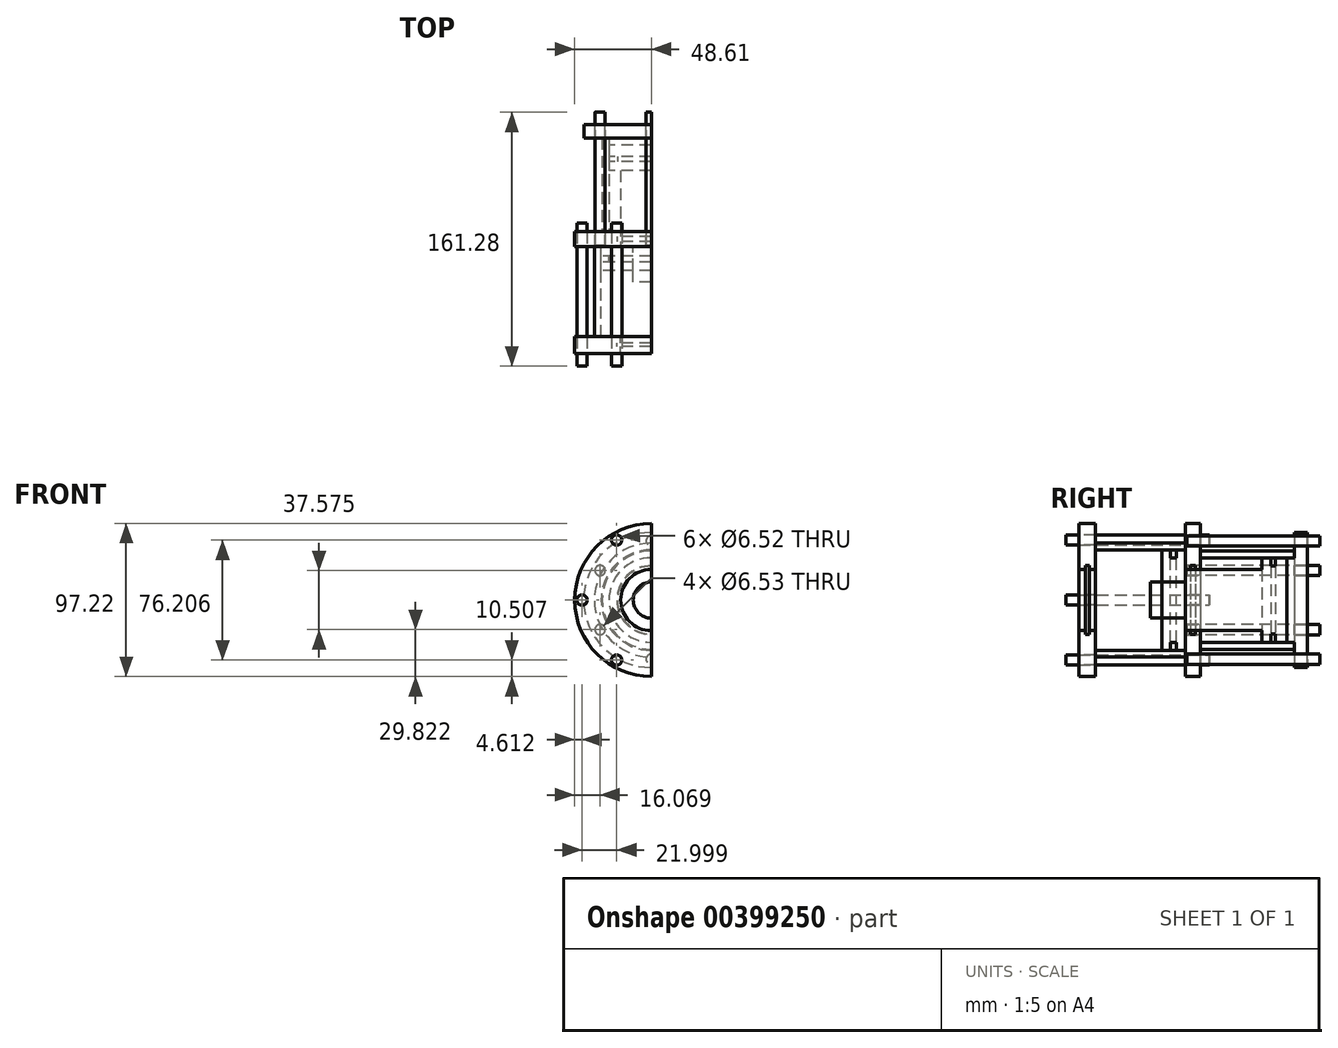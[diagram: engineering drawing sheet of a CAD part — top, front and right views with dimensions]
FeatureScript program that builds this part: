
annotation { "Feature Type Name" : "Feature", "Feature Type Description" : "" }
export const myFeature = defineFeature(function(context is Context, id is Id, definition is map)
    precondition{}
    {
        {
            var Q0;
            Q0=qCreatedBy(makeId("Right.planeOp"),FACE);
            var sketch = newSketch(context, id + "F0", { "sketchPlane" : qUnion([Q0])});
            skLineSegment(sketch, "E0.bottom", {"start": v(0, 0) * mm, "end": v(15.17, 0) * mm});
            skLineSegment(sketch, "E0.top", {"start": v(0, 31.89) * mm, "end": v(15.17, 31.89) * mm});
            skLineSegment(sketch, "E0.left", {"start": v(0, 0) * mm, "end": v(0, 31.89) * mm});
            skLineSegment(sketch, "E0.right", {"start": v(15.17, 0) * mm, "end": v(15.17, 31.89) * mm});
            skLineSegment(sketch, "E1.bottom", {"start": v(15.17, 0) * mm, "end": v(63.65, 0) * mm});
            skLineSegment(sketch, "E1.top", {"start": v(15.17, 19.4) * mm, "end": v(63.65, 19.4) * mm});
            skLineSegment(sketch, "E1.left", {"start": v(15.17, 0) * mm, "end": v(15.17, 19.4) * mm});
            skLineSegment(sketch, "E2.bottom", {"start": v(0, 0) * mm, "end": v(-58.53, 0) * mm});
            skLineSegment(sketch, "E2.top", {"start": v(0, 19.4) * mm, "end": v(-58.53, 19.4) * mm});
            skLineSegment(sketch, "E2.left", {"start": v(0, 0) * mm, "end": v(0, 19.4) * mm});
            skLineSegment(sketch, "E2.right", {"start": v(-58.53, 0) * mm, "end": v(-58.53, 19.4) * mm});
            skLineSegment(sketch, "E3.bottom", {"start": v(15.17, 19.4) * mm, "end": v(24.61, 19.4) * mm});
            skLineSegment(sketch, "E3.top", {"start": v(15.17, 48.61) * mm, "end": v(24.61, 48.61) * mm});
            skLineSegment(sketch, "E3.left", {"start": v(15.17, 19.4) * mm, "end": v(15.17, 48.61) * mm});
            skLineSegment(sketch, "E3.right", {"start": v(24.61, 19.4) * mm, "end": v(24.61, 48.61) * mm});
            skLineSegment(sketch, "E4.bottom", {"start": v(15.17, 31.89) * mm, "end": v(-42, 31.89) * mm});
            skLineSegment(sketch, "E4.top", {"start": v(15.17, 36.17) * mm, "end": v(-42, 36.17) * mm});
            skLineSegment(sketch, "E4.left", {"start": v(15.17, 31.89) * mm, "end": v(15.17, 36.17) * mm});
            skLineSegment(sketch, "E4.right", {"start": v(-42, 31.89) * mm, "end": v(-42, 36.17) * mm});
            skLineSegment(sketch, "E5.bottom", {"start": v(-42, 19.4) * mm, "end": v(-52.7, 19.4) * mm});
            skLineSegment(sketch, "E5.top", {"start": v(-42, 48.61) * mm, "end": v(-52.7, 48.61) * mm});
            skLineSegment(sketch, "E5.left", {"start": v(-42, 19.4) * mm, "end": v(-42, 48.61) * mm});
            skLineSegment(sketch, "E5.right", {"start": v(-52.7, 19.4) * mm, "end": v(-52.7, 48.61) * mm});
            skLineSegment(sketch, "E6.bottom", {"start": v(63.65, 0) * mm, "end": v(84.26, 0) * mm});
            skLineSegment(sketch, "E6.top", {"start": v(63.65, 26.83) * mm, "end": v(84.26, 26.83) * mm});
            skLineSegment(sketch, "E6.left", {"start": v(63.65, 0) * mm, "end": v(63.65, 26.83) * mm});
            skLineSegment(sketch, "E7.bottom", {"start": v(84.26, 0) * mm, "end": v(92.59, 0) * mm});
            skLineSegment(sketch, "E7.top", {"start": v(84.26, 42.86) * mm, "end": v(92.59, 42.86) * mm});
            skLineSegment(sketch, "E7.left", {"start": v(84.26, 26.83) * mm, "end": v(84.26, 42.86) * mm});
            skLineSegment(sketch, "E7.right", {"start": v(92.59, 0) * mm, "end": v(92.59, 42.86) * mm});
            skLineSegment(sketch, "E8.bottom", {"start": v(-48.36, 19.4) * mm, "end": v(-45.88, 19.4) * mm});
            skLineSegment(sketch, "E8.top", {"start": v(-48.36, 21.88) * mm, "end": v(-45.88, 21.88) * mm});
            skLineSegment(sketch, "E8.left", {"start": v(-48.36, 19.4) * mm, "end": v(-48.36, 21.88) * mm});
            skLineSegment(sketch, "E8.right", {"start": v(-45.88, 19.4) * mm, "end": v(-45.88, 21.88) * mm});
            skLineSegment(sketch, "E9.bottom", {"start": v(18.28, 19.4) * mm, "end": v(21.52, 19.4) * mm});
            skLineSegment(sketch, "E9.top", {"start": v(18.28, 21.88) * mm, "end": v(21.52, 21.88) * mm});
            skLineSegment(sketch, "E9.left", {"start": v(18.28, 19.4) * mm, "end": v(18.28, 21.88) * mm});
            skLineSegment(sketch, "E9.right", {"start": v(21.52, 19.4) * mm, "end": v(21.52, 21.88) * mm});
            skLineSegment(sketch, "E10.bottom", {"start": v(5.47, 31.89) * mm, "end": v(9.23, 31.89) * mm});
            skLineSegment(sketch, "E10.top", {"start": v(5.47, 26.83) * mm, "end": v(9.23, 26.83) * mm});
            skLineSegment(sketch, "E10.left", {"start": v(5.47, 31.89) * mm, "end": v(5.47, 26.83) * mm});
            skLineSegment(sketch, "E10.right", {"start": v(9.23, 31.89) * mm, "end": v(9.23, 26.83) * mm});
            skLineSegment(sketch, "E11.bottom", {"start": v(15.17, 11.47) * mm, "end": v(-7.2, 11.47) * mm});
            skLineSegment(sketch, "E11.top", {"start": v(15.17, 0) * mm, "end": v(-7.2, 0) * mm});
            skLineSegment(sketch, "E11.left", {"start": v(15.17, 11.47) * mm, "end": v(15.17, 0) * mm});
            skLineSegment(sketch, "E11.right", {"start": v(-7.2, 11.47) * mm, "end": v(-7.2, 0) * mm});
            skLineSegment(sketch, "E12.bottom", {"start": v(84.26, 26.83) * mm, "end": v(79.61, 26.83) * mm});
            skLineSegment(sketch, "E12.top", {"start": v(82.48, 0) * mm, "end": v(79.61, 0) * mm});
            skLineSegment(sketch, "E12.right", {"start": v(79.61, 26.83) * mm, "end": v(79.61, 0) * mm});
            skLineSegment(sketch, "E13.bottom", {"start": v(84.26, 26.83) * mm, "end": v(24.61, 26.83) * mm});
            skLineSegment(sketch, "E13.top", {"start": v(84.26, 31.23) * mm, "end": v(24.61, 31.23) * mm});
            skLineSegment(sketch, "E13.left", {"start": v(84.26, 26.83) * mm, "end": v(84.26, 31.23) * mm});
            skLineSegment(sketch, "E13.right", {"start": v(24.61, 26.83) * mm, "end": v(24.61, 31.23) * mm});
            skLineSegment(sketch, "E14.bottom", {"start": v(69.32, 26.83) * mm, "end": v(72.3, 26.83) * mm});
            skLineSegment(sketch, "E14.top", {"start": v(69.32, 21.56) * mm, "end": v(72.3, 21.56) * mm});
            skLineSegment(sketch, "E14.left", {"start": v(69.32, 26.83) * mm, "end": v(69.32, 21.56) * mm});
            skLineSegment(sketch, "E14.right", {"start": v(72.3, 26.83) * mm, "end": v(72.3, 21.56) * mm});
            skSolve(sketch);
        }
        {
            var Q0;
            Q0=makeQuery(id+"F0.imprint","IMPRINT",FACE,{"disambiguationData":[TD([[makeQuery(id+"F0.imprint","IMPRINT",EDGE,{"derivedFrom":sQuery(id+"F0.wireOp",EDGE,"E2.bottom")}),-1.0]])]});
            var Q1;
            {var subQ6=sQuery(id+"F0.wireOp",EDGE,"E0.left");Q1=makeQuery(id+"F0.imprint","IMPRINT",FACE,{"disambiguationData":[TD([[makeQuery(id+"F0.imprint","IMPRINT",EDGE,{"derivedFrom":subQ6}),-1.0]])]});}
            var Q2;
            Q2=sQuery(id+"F0.wireOp",EDGE,"E2.bottom");
            revolve(context, id + "F1", {"entities" : qUnion([Q0, Q1]), "axis" : qUnion([Q2]), "revolveType" : RevolveType.FULL});
        }
        {
            var Q0;
            {var subQ4=sQuery(id+"F0.wireOp",EDGE,"E1.bottom");Q0=makeQuery(id+"F0.imprint","IMPRINT",FACE,{"disambiguationData":[TD([[makeQuery(id+"F0.imprint","IMPRINT",EDGE,{"derivedFrom":subQ4}),1.0]])]});}
            var Q1;
            {var subQ5=sQuery(id+"F0.wireOp",EDGE,"E11.left");Q1=makeQuery(id+"F0.imprint","IMPRINT",FACE,{"disambiguationData":[TD([[makeQuery(id+"F0.imprint","IMPRINT",EDGE,{"derivedFrom":subQ5}),-1.0]])]});}
            var Q2;
            {var subQ4=sQuery(id+"F0.wireOp",EDGE,"E12.right");Q2=makeQuery(id+"F0.imprint","IMPRINT",FACE,{"disambiguationData":[TD([[makeQuery(id+"F0.imprint","IMPRINT",EDGE,{"derivedFrom":subQ4}),-1.0]])]});}
            var Q3;
            Q3=sQuery(id+"F0.wireOp",EDGE,"E1.bottom");
            revolve(context, id + "F2", {"entities" : qUnion([Q0, Q1, Q2]), "axis" : qUnion([Q3]), "revolveType" : RevolveType.FULL});
        }
        {
            var Q0;
            {var subQ5=sQuery(id+"F0.wireOp",EDGE,"E5.top");Q0=makeQuery(id+"F0.imprint","IMPRINT",FACE,{"disambiguationData":[TD([[makeQuery(id+"F0.imprint","IMPRINT",EDGE,{"derivedFrom":subQ5}),1.0]])]});}
            var Q1;
            Q1=sQuery(id+"F0.wireOp",EDGE,"E2.bottom");
            revolve(context, id + "F3", {"entities" : qUnion([Q0]), "axis" : qUnion([Q1]), "revolveType" : RevolveType.FULL});
        }
        {
            var Q0;
            {var subQ2=sQuery(id+"F0.wireOp",EDGE,"E3.top");Q0=makeQuery(id+"F0.imprint","IMPRINT",FACE,{"disambiguationData":[TD([[makeQuery(id+"F0.imprint","IMPRINT",EDGE,{"derivedFrom":subQ2}),-1.0]])]});}
            var Q1;
            Q1=sQuery(id+"F0.wireOp",EDGE,"E1.bottom");
            revolve(context, id + "F4", {"entities" : qUnion([Q0]), "axis" : qUnion([Q1]), "revolveType" : RevolveType.FULL});
        }
        {
            var Q0;
            {var subQ3=sQuery(id+"F0.wireOp",EDGE,"E7.bottom");Q0=makeQuery(id+"F0.imprint","IMPRINT",FACE,{"disambiguationData":[TD([[makeQuery(id+"F0.imprint","IMPRINT",EDGE,{"derivedFrom":subQ3}),1.0]])]});}
            var Q1;
            Q1=sQuery(id+"F0.wireOp",EDGE,"E1.bottom");
            revolve(context, id + "F5", {"entities" : qUnion([Q0]), "axis" : qUnion([Q1]), "revolveType" : RevolveType.FULL});
        }
        {
            var Q0;
            {var subQ0=sQuery(id+"F0.wireOp",EDGE,"E4.top");Q0=makeQuery(id+"F0.imprint","IMPRINT",FACE,{"disambiguationData":[TD([[makeQuery(id+"F0.imprint","IMPRINT",EDGE,{"derivedFrom":subQ0}),1.0]])]});}
            var Q1;
            Q1=sQuery(id+"F0.wireOp",EDGE,"E2.bottom");
            revolve(context, id + "F6", {"entities" : qUnion([Q0]), "axis" : qUnion([Q1]), "revolveType" : RevolveType.FULL});
        }
        {
            var Q0;
            Q0=makeQuery(id+"F0.imprint","IMPRINT",FACE,{"disambiguationData":[TD([[makeQuery(id+"F0.imprint","IMPRINT",EDGE,{"derivedFrom":sQuery(id+"F0.wireOp",EDGE,"E13.top")}),1.0]])]});
            var Q1;
            Q1=sQuery(id+"F0.wireOp",EDGE,"E1.bottom");
            revolve(context, id + "F7", {"entities" : qUnion([Q0]), "axis" : qUnion([Q1]), "revolveType" : RevolveType.FULL});
        }
        {
            var Q0;
            Q0=makeQuery(id+"F5.opRevolve","SWEPT_FACE",FACE,{"disambiguationData":[OSD([sQuery(id+"F0.wireOp",EDGE,"E7.right")])]});
            var sketch = newSketch(context, id + "F8", { "sketchPlane" : qUnion([Q0])});
            skCircle(sketch, "E15", {"center": v(0, 37.57) * mm, "radius": 3.27 * mm});
            skCircle(sketch, "E16.1.0", {"center": v(-32.54, 18.79) * mm, "radius": 3.27 * mm});
            skCircle(sketch, "E16.2.0", {"center": v(-32.54, -18.79) * mm, "radius": 3.27 * mm});
            skCircle(sketch, "E16.3.0", {"center": v(0, -37.57) * mm, "radius": 3.27 * mm});
            skCircle(sketch, "E16.4.0", {"center": v(32.54, -18.79) * mm, "radius": 3.27 * mm});
            skCircle(sketch, "E16.5.0", {"center": v(32.54, 18.79) * mm, "radius": 3.27 * mm});
            skPoint(sketch, "E16.center", {"position": v(0, 0) * mm});
            skSolve(sketch);
        }
        {
            var Q0;
            Q0=makeQuery(id+"F8.imprint","IMPRINT",FACE,{"disambiguationData":[TD([[makeQuery(id+"F8.imprint","IMPRINT",EDGE,{"derivedFrom":sQuery(id+"F8.wireOp",EDGE,"E16.1.0")}),1.0]])]});
            var Q1;
            Q1=makeQuery(id+"F8.imprint","IMPRINT",FACE,{"disambiguationData":[TD([[makeQuery(id+"F8.imprint","IMPRINT",EDGE,{"derivedFrom":sQuery(id+"F8.wireOp",EDGE,"E15")}),1.0]])]});
            var Q2;
            Q2=makeQuery(id+"F8.imprint","IMPRINT",FACE,{"disambiguationData":[TD([[makeQuery(id+"F8.imprint","IMPRINT",EDGE,{"derivedFrom":sQuery(id+"F8.wireOp",EDGE,"E16.5.0")}),1.0]])]});
            var Q3;
            Q3=makeQuery(id+"F8.imprint","IMPRINT",FACE,{"disambiguationData":[TD([[makeQuery(id+"F8.imprint","IMPRINT",EDGE,{"derivedFrom":sQuery(id+"F8.wireOp",EDGE,"E16.4.0")}),1.0]])]});
            var Q4;
            Q4=makeQuery(id+"F8.imprint","IMPRINT",FACE,{"disambiguationData":[TD([[makeQuery(id+"F8.imprint","IMPRINT",EDGE,{"derivedFrom":sQuery(id+"F8.wireOp",EDGE,"E16.3.0")}),1.0]])]});
            var Q5;
            Q5=makeQuery(id+"F8.imprint","IMPRINT",FACE,{"disambiguationData":[TD([[makeQuery(id+"F8.imprint","IMPRINT",EDGE,{"derivedFrom":sQuery(id+"F8.wireOp",EDGE,"E16.2.0")}),1.0]])]});
            var Q6;
            Q6=makeQuery(id+"F4.opRevolve","SWEPT_FACE",FACE,{"disambiguationData":[OSD([sQuery(id+"F0.wireOp",EDGE,"E3.left"),sQuery(id+"F0.wireOp",EDGE,"E4.left")])]});
            extrude(context, id + "F9", {"entities" : qUnion([Q0, Q1, Q2, Q3, Q4, Q5]), "operationType" : NewBodyOperationType.REMOVE, "endBound" : BoundingType.UP_TO_SURFACE, "oppositeDirection" : true, "endBoundEntityFace" : qUnion([Q6]), "depth" : 25 * mm});
        }
        {
            var Q0;
            Q0=makeQuery(id+"F3.opRevolve","SWEPT_FACE",FACE,{"disambiguationData":[OSD([sQuery(id+"F0.wireOp",EDGE,"E5.right")])]});
            var sketch = newSketch(context, id + "F10", { "sketchPlane" : qUnion([Q0])});
            skLineSegment(sketch, "E17", {"start": v(0, 0) * mm, "end": v(24.3, 42.1) * mm});
            skCircle(sketch, "E18", {"center": v(22, 38.1) * mm, "radius": 3.26 * mm});
            skCircle(sketch, "E19.1.0", {"center": v(-22, 38.1) * mm, "radius": 3.26 * mm});
            skCircle(sketch, "E19.2.0", {"center": v(-44, 0) * mm, "radius": 3.26 * mm});
            skCircle(sketch, "E19.3.0", {"center": v(-22, -38.1) * mm, "radius": 3.26 * mm});
            skCircle(sketch, "E19.4.0", {"center": v(22, -38.1) * mm, "radius": 3.26 * mm});
            skCircle(sketch, "E19.5.0", {"center": v(44, 0) * mm, "radius": 3.26 * mm});
            skPoint(sketch, "E19.center", {"position": v(0, 0) * mm});
            skSolve(sketch);
        }
        {
            var Q0;
            Q0=makeQuery(id+"F10.imprint","IMPRINT",FACE,{"disambiguationData":[TD([[makeQuery(id+"F10.imprint","IMPRINT",EDGE,{"derivedFrom":sQuery(id+"F10.wireOp",EDGE,"E19.1.0")}),1.0]])]});
            var Q1;
            Q1=makeQuery(id+"F10.imprint","IMPRINT",FACE,{"disambiguationData":[TD([[makeQuery(id+"F10.imprint","IMPRINT",EDGE,{"derivedFrom":sQuery(id+"F10.wireOp",EDGE,"E19.2.0")}),1.0]])]});
            var Q2;
            Q2=makeQuery(id+"F10.imprint","IMPRINT",FACE,{"disambiguationData":[TD([[makeQuery(id+"F10.imprint","IMPRINT",EDGE,{"derivedFrom":sQuery(id+"F10.wireOp",EDGE,"E19.3.0")}),1.0]])]});
            var Q3;
            Q3=makeQuery(id+"F10.imprint","IMPRINT",FACE,{"disambiguationData":[TD([[makeQuery(id+"F10.imprint","IMPRINT",EDGE,{"derivedFrom":sQuery(id+"F10.wireOp",EDGE,"E19.4.0")}),1.0]])]});
            var Q4;
            Q4=makeQuery(id+"F10.imprint","IMPRINT",FACE,{"disambiguationData":[TD([[makeQuery(id+"F10.imprint","IMPRINT",EDGE,{"derivedFrom":sQuery(id+"F10.wireOp",EDGE,"E19.5.0")}),1.0]])]});
            var Q5;
            {var subQ0=sQuery(id+"F10.wireOp",EDGE,"E18");var subQ1=sQuery(id+"F10.wireOp",EDGE,"E17");var subQ2=makeQuery(id+"F10.imprint","INTERSECT",VERTEX,{"disambiguationData":[OD(0.0)],"derivedFrom":[subQ1,subQ0]});Q5=makeQuery(id+"F10.imprint","IMPRINT",FACE,{"disambiguationData":[TD([[makeQuery(id+"F10.imprint","IMPRINT",EDGE,{"disambiguationData":[TD([[subQ2,-1.0]])],"derivedFrom":subQ1}),-1.0]])]});}
            var Q6;
            {var subQ0=sQuery(id+"F10.wireOp",EDGE,"E18");var subQ1=sQuery(id+"F10.wireOp",EDGE,"E17");var subQ2=makeQuery(id+"F10.imprint","INTERSECT",VERTEX,{"disambiguationData":[OD(0.0)],"derivedFrom":[subQ1,subQ0]});Q6=makeQuery(id+"F10.imprint","IMPRINT",FACE,{"disambiguationData":[TD([[makeQuery(id+"F10.imprint","IMPRINT",EDGE,{"disambiguationData":[TD([[subQ2,-1.0]])],"derivedFrom":subQ1}),1.0]])]});}
            var Q7;
            Q7=makeQuery(id+"F4.opRevolve","SWEPT_FACE",FACE,{"disambiguationData":[OSD([sQuery(id+"F0.wireOp",EDGE,"E3.right"),sQuery(id+"F0.wireOp",EDGE,"lStvYGKo-UQwx-T2YS-vUQB-Xu7iDgR6D970.right")])]});
            extrude(context, id + "F11", {"entities" : qUnion([Q0, Q1, Q2, Q3, Q4, Q5, Q6]), "operationType" : NewBodyOperationType.REMOVE, "endBound" : BoundingType.UP_TO_SURFACE, "oppositeDirection" : true, "endBoundEntityFace" : qUnion([Q7]), "depth" : 25 * mm});
        }
        {
            var Q0;
            Q0=makeQuery(id+"F10.imprint","IMPRINT",FACE,{"disambiguationData":[TD([[makeQuery(id+"F10.imprint","IMPRINT",EDGE,{"derivedFrom":sQuery(id+"F10.wireOp",EDGE,"E19.1.0")}),1.0]])]});
            var Q1;
            Q1=makeQuery(id+"F4.opRevolve","SWEPT_FACE",FACE,{"disambiguationData":[OSD([sQuery(id+"F0.wireOp",EDGE,"E3.right"),sQuery(id+"F0.wireOp",EDGE,"lStvYGKo-UQwx-T2YS-vUQB-Xu7iDgR6D970.right")])]});
            extrude(context, id + "F12", {"entities" : qUnion([Q0]), "depth" : 8 * mm, "hasSecondDirection" : true, "secondDirectionOppositeDirection" : true, "secondDirectionBoundEntityFace" : qUnion([Q1]), "secondDirectionDepth" : 83 * mm});
        }
        {
            var Q0;
            Q0=makeQuery(id+"F12.opExtrude","SWEPT_BODY",BODY,{"disambiguationData":[OSD([sQuery(id+"F10.wireOp",EDGE,"E19.1.0")])]});
            var Q1;
            Q1=sQuery(id+"F0.wireOp",EDGE,"E1.bottom");
            circularPattern(context, id + "F13", {"entities" : qUnion([Q0]), "axis" : qUnion([Q1]), "angle" : 360 * degree, "instanceCount" : 6, "equalSpace" : true});
        }
        {
            var Q0;
            Q0=makeQuery(id+"F8.imprint","IMPRINT",FACE,{"disambiguationData":[TD([[makeQuery(id+"F8.imprint","IMPRINT",EDGE,{"derivedFrom":sQuery(id+"F8.wireOp",EDGE,"E15")}),1.0]])]});
            extrude(context, id + "F14", {"entities" : qUnion([Q0]), "depth" : 8 * mm, "hasSecondDirection" : true, "secondDirectionOppositeDirection" : true, "secondDirectionDepth" : 76.7 * mm});
        }
        {
            var Q0;
            Q0=makeQuery(id+"F14.opExtrude","SWEPT_BODY",BODY,{"disambiguationData":[OSD([sQuery(id+"F8.wireOp",EDGE,"E15")])]});
            var Q1;
            Q1=sQuery(id+"F0.wireOp",EDGE,"E6.bottom");
            circularPattern(context, id + "F15", {"entities" : qUnion([Q0]), "axis" : qUnion([Q1]), "angle" : 360 * degree, "instanceCount" : 6, "equalSpace" : true});
        }
        {
            var Q0;
            Q0=qCreatedBy(makeId("Front.planeOp"),FACE);
            var sketch = newSketch(context, id + "F16", { "sketchPlane" : qUnion([Q0])});
            skLineSegment(sketch, "E20.bottom", {"start": v(0, -52.7) * mm, "end": v(57.56, -52.7) * mm});
            skLineSegment(sketch, "E20.top", {"start": v(0, 54.06) * mm, "end": v(57.56, 54.06) * mm});
            skLineSegment(sketch, "E20.left", {"start": v(0, -52.7) * mm, "end": v(0, 54.06) * mm});
            skLineSegment(sketch, "E20.right", {"start": v(57.56, -52.7) * mm, "end": v(57.56, 54.06) * mm});
            skSolve(sketch);
        }
        {
            var Q0;
            Q0=makeQuery(id+"F16.imprint","IMPRINT",FACE,{"disambiguationData":[TD([[makeQuery(id+"F16.imprint","IMPRINT",EDGE,{"derivedFrom":sQuery(id+"F16.wireOp",EDGE,"E20.bottom")}),1.0]])]});
            extrude(context, id + "F17", {"entities" : qUnion([Q0]), "operationType" : NewBodyOperationType.REMOVE, "endBound" : BoundingType.THROUGH_ALL, "oppositeDirection" : true, "depth" : 25 * mm, "hasSecondDirection" : true, "secondDirectionBound" : SecondDirectionBoundingType.THROUGH_ALL, "secondDirectionOppositeDirection" : false, "secondDirectionDepth" : 25 * mm});
        }
    });
